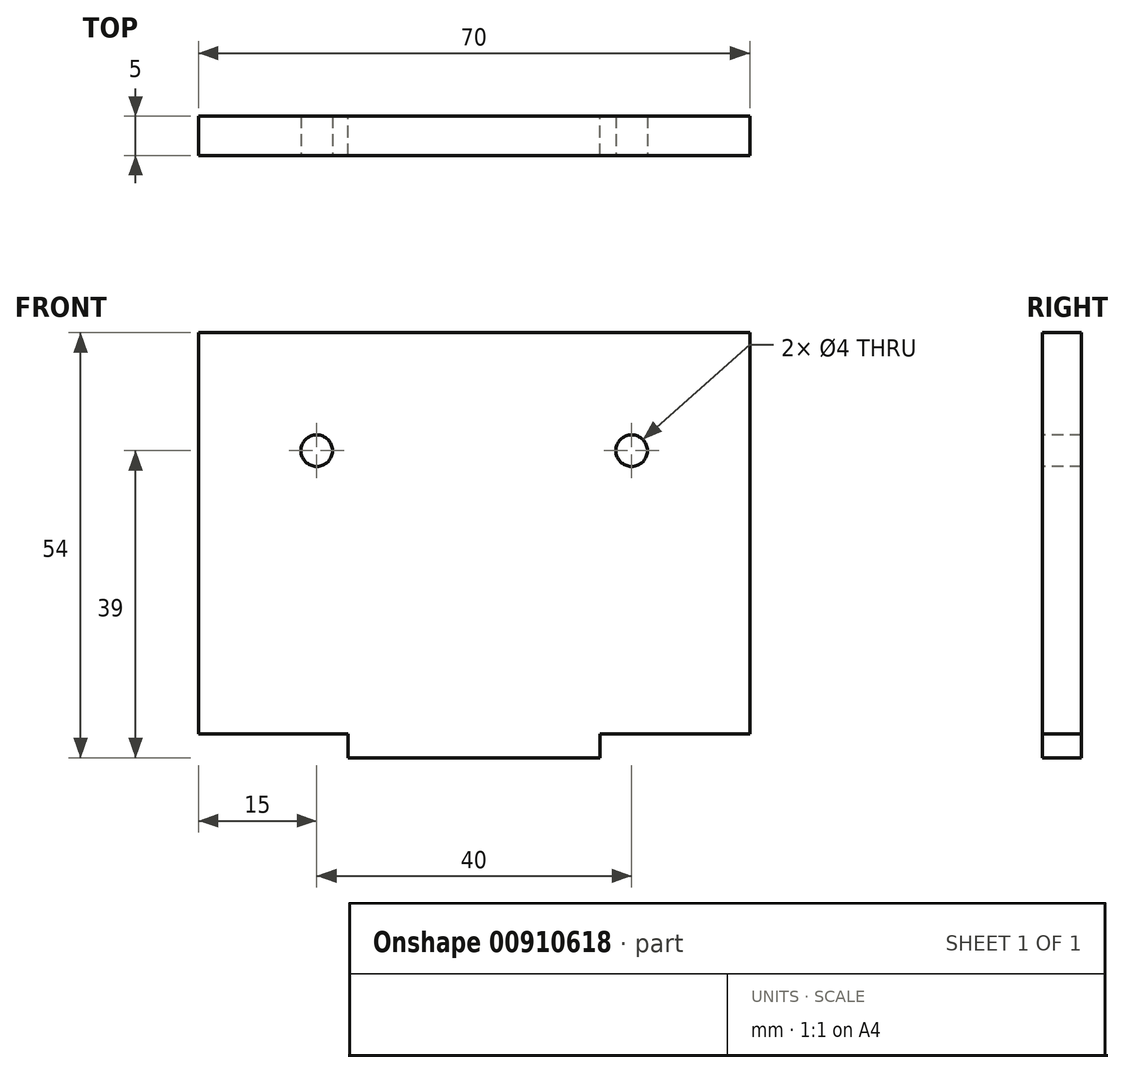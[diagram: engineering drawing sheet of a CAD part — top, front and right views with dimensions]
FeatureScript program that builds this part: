
annotation { "Feature Type Name" : "Feature", "Feature Type Description" : "" }
export const myFeature = defineFeature(function(context is Context, id is Id, definition is map)
    precondition{}
    {
        {
            var Q0;
            Q0=qCreatedBy(makeId("Front.planeOp"),FACE);
            var sketch = newSketch(context, id + "F0", { "sketchPlane" : qUnion([Q0])});
            skLineSegment(sketch, "E0.bottom", {"start": v(35, 25.5) * mm, "end": v(-35, 25.5) * mm});
            skLineSegment(sketch, "E0.left", {"start": v(35, 25.5) * mm, "end": v(35, -25.5) * mm});
            skLineSegment(sketch, "E0.right", {"start": v(-35, 25.5) * mm, "end": v(-35, -25.5) * mm});
            skPoint(sketch, "E0.middle", {"position": v(0, 0) * mm});
            skLineSegment(sketch, "E1.top", {"start": v(16, -28.5) * mm, "end": v(-16, -28.5) * mm});
            skLineSegment(sketch, "E2", {"start": v(-35, -25.5) * mm, "end": v(-16, -25.5) * mm});
            skLineSegment(sketch, "E3", {"start": v(35, -25.5) * mm, "end": v(16, -25.5) * mm});
            skLineSegment(sketch, "E4", {"start": v(16, -25.5) * mm, "end": v(16, -28.5) * mm});
            skLineSegment(sketch, "E5", {"start": v(-16, -25.5) * mm, "end": v(-16, -28.5) * mm});
            skSolve(sketch);
        }
        {
            var Q0;
            Q0 = qSketchRegion(id + "F0", true);
            extrude(context, id + "F1", {"entities" : qUnion([Q0]), "depth" : 5 * mm, "offsetDistance" : 25 * mm});
        }
        {
            var Q0;
            Q0=makeQuery(id+"F1.opExtrude","CAP_FACE",FACE,{"disambiguationData":[OSD([sQuery(id+"F0.wireOp",EDGE,"E0.bottom"),sQuery(id+"F0.wireOp",EDGE,"E0.left"),sQuery(id+"F0.wireOp",EDGE,"E0.right"),sQuery(id+"F0.wireOp",EDGE,"E1.top"),sQuery(id+"F0.wireOp",EDGE,"E2"),sQuery(id+"F0.wireOp",EDGE,"E3"),sQuery(id+"F0.wireOp",EDGE,"E4"),sQuery(id+"F0.wireOp",EDGE,"E5")])],"isStart":false});
            var sketch = newSketch(context, id + "F2", { "sketchPlane" : qUnion([Q0])});
            skCircle(sketch, "E6", {"center": v(-20, 10.5) * mm, "radius": 2 * mm});
            skCircle(sketch, "E7", {"center": v(20, 10.5) * mm, "radius": 2 * mm});
            skSolve(sketch);
        }
        {
            var Q0;
            Q0 = qSketchRegion(id + "F2", true);
            extrude(context, id + "F3", {"entities" : qUnion([Q0]), "operationType" : NewBodyOperationType.REMOVE, "oppositeDirection" : true, "depth" : 25 * mm, "offsetDistance" : 25 * mm});
        }
    });
